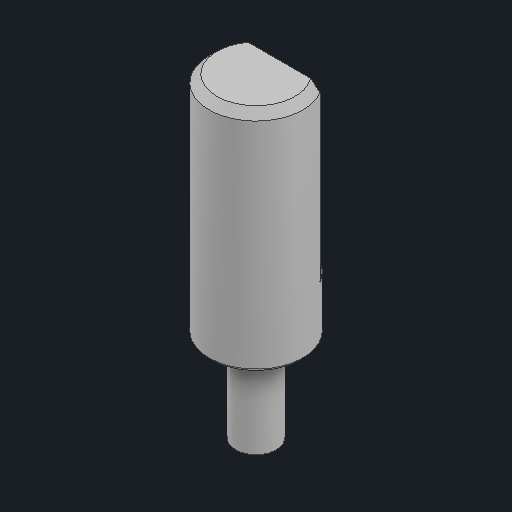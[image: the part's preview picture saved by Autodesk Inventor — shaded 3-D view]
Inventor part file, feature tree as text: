
AUTODESK INVENTOR PART (.ipt)
format: ipt  version: 2023 (Build 270158000, 158)  size: 100,352 bytes
history: mixed  units: in
note: dims shown in document units (in); Inventor stores cm internally (conversion verified against a paired STEP export)
features: chamfer x1, imported_body x1
ambient origin geometry x8: Origin, YZ Plane, XZ Plane, XY Plane, X Axis, Y Axis, Z Axis, Center Point
bodies: Solid1 (imported_parasolid)
feature tree (2):
  chamfer  "倒角2"  [1 undecoded]
  imported_body  NMx_Import_Brep_tag  [imported B-rep: ~9 faces, bbox_mm=[5.196152, 20.2, 4.5]]
note: 1 required parameter value undecoded (feature->parameter linkage not recoverable at this tier; creation-order binding heuristic only, values carry confidence <= 0.55)
